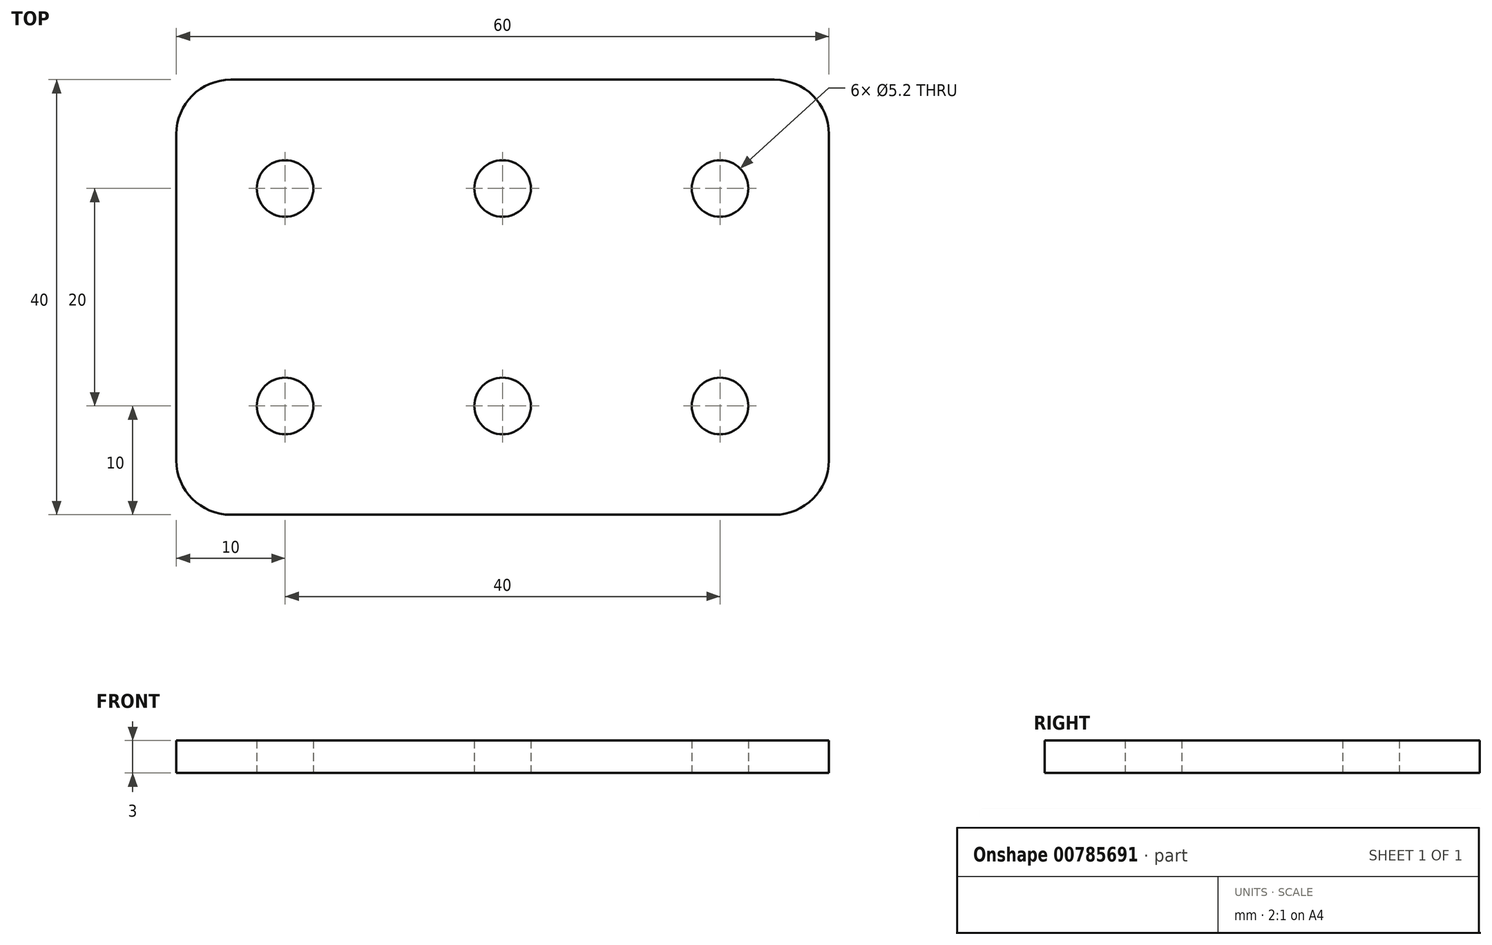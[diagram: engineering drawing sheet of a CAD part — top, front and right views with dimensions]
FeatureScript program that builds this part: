
annotation { "Feature Type Name" : "Feature", "Feature Type Description" : "" }
export const myFeature = defineFeature(function(context is Context, id is Id, definition is map)
    precondition{}
    {
        {
            var Q0;
            Q0=qCreatedBy(makeId("Top.planeOp"),FACE);
            var sketch = newSketch(context, id + "F0", { "sketchPlane" : qUnion([Q0])});
            skLineSegment(sketch, "E0.bottom", {"start": v(25, -20) * mm, "end": v(-25, -20) * mm});
            skLineSegment(sketch, "E0.top", {"start": v(25, 20) * mm, "end": v(-25, 20) * mm});
            skLineSegment(sketch, "E0.left", {"start": v(30, -15) * mm, "end": v(30, 15) * mm});
            skLineSegment(sketch, "E0.right", {"start": v(-30, -15) * mm, "end": v(-30, 15) * mm});
            skPoint(sketch, "E0.middle", {"position": v(0, 0) * mm});
            skPoint(sketch, "E1.visualSharp", {"position": v(-30, 20) * mm});
            skArc(sketch, "E1.filletArc", {"start": v(-25, 20) * mm, "mid": v(-28.54, 18.54) * mm, "end": v(-30, 15) * mm});
            skPoint(sketch, "E2.visualSharp", {"position": v(-30, -20) * mm});
            skArc(sketch, "E2.filletArc", {"start": v(-30, -15) * mm, "mid": v(-28.54, -18.54) * mm, "end": v(-25, -20) * mm});
            skPoint(sketch, "E3.visualSharp", {"position": v(30, -20) * mm});
            skArc(sketch, "E3.filletArc", {"start": v(25, -20) * mm, "mid": v(28.54, -18.54) * mm, "end": v(30, -15) * mm});
            skPoint(sketch, "E4.visualSharp", {"position": v(30, 20) * mm});
            skArc(sketch, "E4.filletArc", {"start": v(30, 15) * mm, "mid": v(28.54, 18.54) * mm, "end": v(25, 20) * mm});
            skLineSegment(sketch, "E5", {"start": v(-38.14, 10) * mm, "end": v(40.61, 10) * mm, "construction": true});
            skLineSegment(sketch, "E6", {"start": v(-20, 33.18) * mm, "end": v(-20, -33.73) * mm, "construction": true});
            skCircle(sketch, "E7", {"center": v(-20, 10) * mm, "radius": 2.6 * mm});
            skCircle(sketch, "E8.0.1.0", {"center": v(-20, -10) * mm, "radius": 2.6 * mm});
            skCircle(sketch, "E8.1.0.0", {"center": v(0, 10) * mm, "radius": 2.6 * mm});
            skCircle(sketch, "E8.1.1.0", {"center": v(0, -10) * mm, "radius": 2.6 * mm});
            skLineSegment(sketch, "E8.direction1", {"start": v(-20, 10) * mm, "end": v(0, 10) * mm, "construction": true});
            skLineSegment(sketch, "E8.direction2", {"start": v(-20, 10) * mm, "end": v(-20, -10) * mm, "construction": true});
            skCircle(sketch, "E9.0.2.0", {"center": v(20, 10) * mm, "radius": 2.6 * mm});
            skCircle(sketch, "E9.0.2.1", {"center": v(20, -10) * mm, "radius": 2.6 * mm});
            skSolve(sketch);
        }
        {
            var Q0;
            Q0=makeQuery(id+"F0.imprint","IMPRINT",FACE,{"disambiguationData":[TD([[makeQuery(id+"F0.imprint","IMPRINT",EDGE,{"derivedFrom":sQuery(id+"F0.wireOp",EDGE,"E0.bottom")}),-1.0]])]});
            extrude(context, id + "F1", {"entities" : qUnion([Q0]), "depth" : 3 * mm, "offsetDistance" : 25 * mm});
        }
    });
